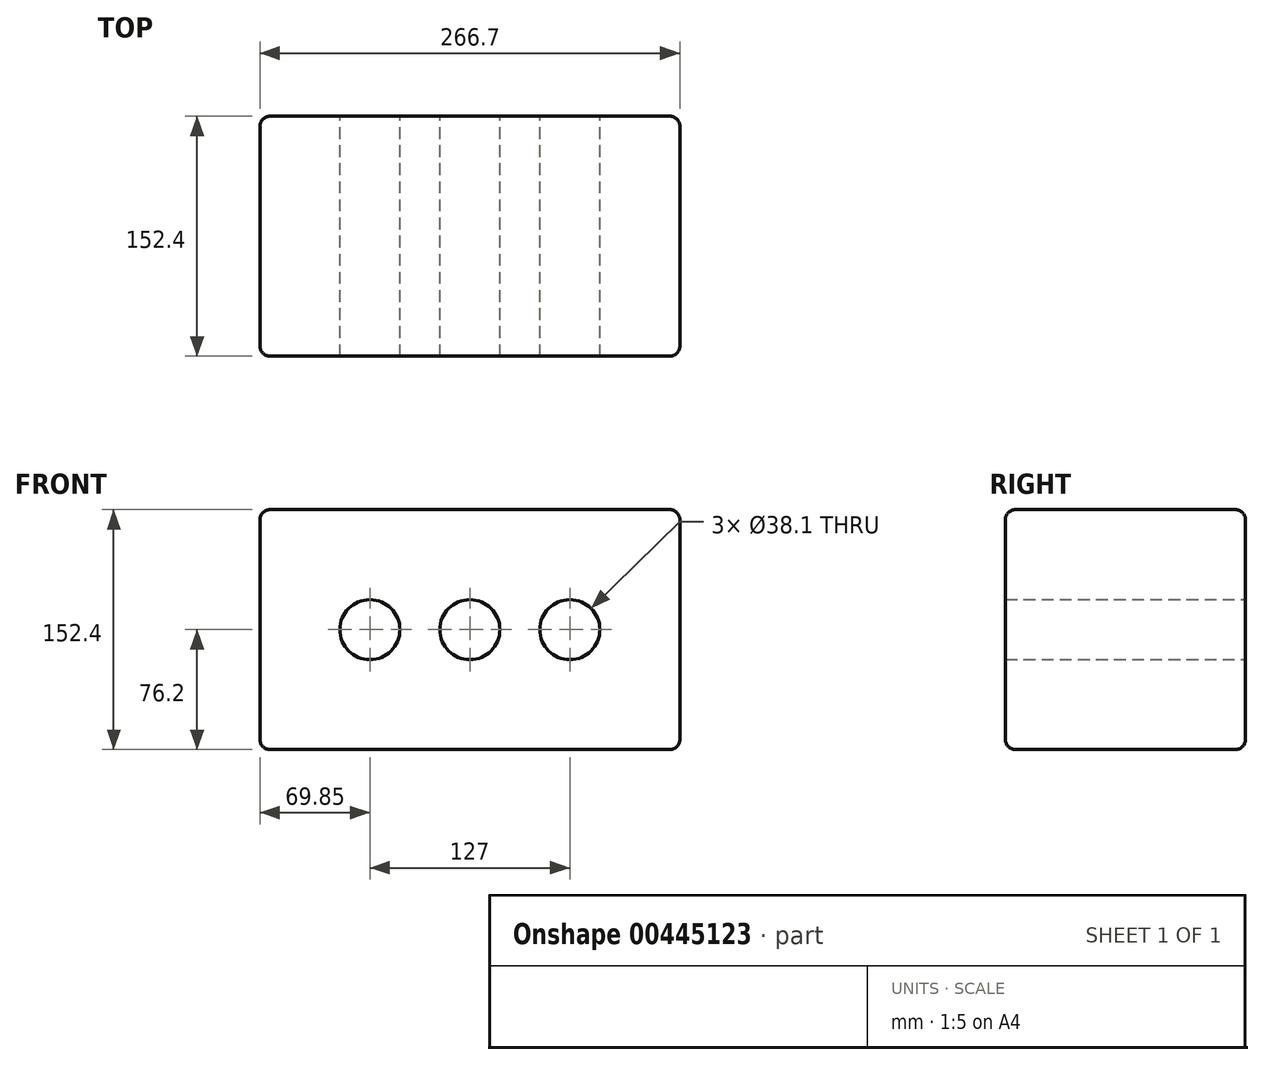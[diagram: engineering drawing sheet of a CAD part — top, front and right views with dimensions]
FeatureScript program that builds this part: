
annotation { "Feature Type Name" : "Feature", "Feature Type Description" : "" }
export const myFeature = defineFeature(function(context is Context, id is Id, definition is map)
    precondition{}
    {
        {
            var Q0;
            Q0=qCreatedBy(makeId("Front.planeOp"),FACE);
            var sketch = newSketch(context, id + "F0", { "sketchPlane" : qUnion([Q0])});
            skLineSegment(sketch, "E0.bottom", {"start": v(133.35, -76.2) * mm, "end": v(-133.35, -76.2) * mm});
            skLineSegment(sketch, "E0.top", {"start": v(133.35, 76.2) * mm, "end": v(-133.35, 76.2) * mm});
            skLineSegment(sketch, "E0.left", {"start": v(133.35, -76.2) * mm, "end": v(133.35, 76.2) * mm});
            skLineSegment(sketch, "E0.right", {"start": v(-133.35, -76.2) * mm, "end": v(-133.35, 76.2) * mm});
            skPoint(sketch, "E0.middle", {"position": v(0, 0) * mm});
            skCircle(sketch, "E1", {"center": v(-63.5, 0) * mm, "radius": 19.05 * mm});
            skCircle(sketch, "E2", {"center": v(0, 0) * mm, "radius": 19.05 * mm});
            skCircle(sketch, "E3", {"center": v(63.5, 0) * mm, "radius": 19.05 * mm});
            skLineSegment(sketch, "E4", {"start": v(-133.35, 0) * mm, "end": v(-82.55, 0) * mm});
            skLineSegment(sketch, "E5", {"start": v(-44.45, 0) * mm, "end": v(-19.05, 0) * mm});
            skLineSegment(sketch, "E6", {"start": v(19.05, 0) * mm, "end": v(44.45, 0) * mm});
            skLineSegment(sketch, "E7", {"start": v(82.55, 0) * mm, "end": v(133.35, 0) * mm});
            skLineSegment(sketch, "E8", {"start": v(-63.5, 0) * mm, "end": v(0, 0) * mm});
            skLineSegment(sketch, "E9", {"start": v(63.5, 0) * mm, "end": v(0, 0) * mm});
            skSolve(sketch);
        }
        {
            var Q0;
            {var subQ1=sQuery(id+"F0.wireOp",EDGE,"E0.bottom");Q0=makeQuery(id+"F0.imprint","IMPRINT",FACE,{"disambiguationData":[TD([[makeQuery(id+"F0.imprint","IMPRINT",EDGE,{"derivedFrom":subQ1}),-1.0]])]});}
            var Q1;
            {var subQ1=sQuery(id+"F0.wireOp",EDGE,"E0.top");Q1=makeQuery(id+"F0.imprint","IMPRINT",FACE,{"disambiguationData":[TD([[makeQuery(id+"F0.imprint","IMPRINT",EDGE,{"derivedFrom":subQ1}),1.0]])]});}
            extrude(context, id + "F1", {"entities" : qUnion([Q0, Q1]), "depth" : 152.4 * mm});
        }
        {
            var Q0;
            Q0=makeQuery(id+"F1.opExtrude","CAP_EDGE",EDGE,{"disambiguationData":[OSD([sQuery(id+"F0.wireOp",EDGE,"E0.top")])],"isStart":false});
            var Q1;
            Q1=makeQuery(id+"F1.opExtrude","CAP_EDGE",EDGE,{"disambiguationData":[OSD([sQuery(id+"F0.wireOp",EDGE,"E0.left")])],"isStart":false});
            var Q2;
            Q2=makeQuery(id+"F1.opExtrude","CAP_EDGE",EDGE,{"disambiguationData":[OSD([sQuery(id+"F0.wireOp",EDGE,"E0.right")])],"isStart":false});
            var Q3;
            Q3=makeQuery(id+"F1.opExtrude","CAP_EDGE",EDGE,{"disambiguationData":[OSD([sQuery(id+"F0.wireOp",EDGE,"E0.bottom")])],"isStart":false});
            var Q4;
            Q4=makeQuery(id+"F1.opExtrude","CAP_EDGE",EDGE,{"disambiguationData":[OSD([sQuery(id+"F0.wireOp",EDGE,"E0.left")])],"isStart":true});
            var Q5;
            Q5=makeQuery(id+"F1.opExtrude","SWEPT_EDGE",EDGE,{"disambiguationData":[OSD([sQuery(id+"F0.wireOp",EDGE,"E0.bottom"),sQuery(id+"F0.wireOp",EDGE,"E0.left")])]});
            var Q6;
            Q6=makeQuery(id+"F1.opExtrude","SWEPT_EDGE",EDGE,{"disambiguationData":[OSD([sQuery(id+"F0.wireOp",EDGE,"E0.top"),sQuery(id+"F0.wireOp",EDGE,"E0.left")])]});
            var Q7;
            Q7=makeQuery(id+"F1.opExtrude","SWEPT_FACE",FACE,{"disambiguationData":[OSD([sQuery(id+"F0.wireOp",EDGE,"E0.top")])]});
            var Q8;
            Q8=makeQuery(id+"F1.opExtrude","SWEPT_EDGE",EDGE,{"disambiguationData":[OSD([sQuery(id+"F0.wireOp",EDGE,"E0.bottom"),sQuery(id+"F0.wireOp",EDGE,"E0.right")])]});
            var Q9;
            Q9=makeQuery(id+"F1.opExtrude","CAP_EDGE",EDGE,{"disambiguationData":[OSD([sQuery(id+"F0.wireOp",EDGE,"E0.right")])],"isStart":true});
            var Q10;
            Q10=makeQuery(id+"F1.opExtrude","CAP_EDGE",EDGE,{"disambiguationData":[OSD([sQuery(id+"F0.wireOp",EDGE,"E0.bottom")])],"isStart":true});
            fillet(context, id + "F2", {"entities" : qUnion([Q0, Q1, Q2, Q3, Q4, Q5, Q6, Q7, Q8, Q9, Q10]), "radius" : 6.35 * mm, "tangentPropagation" : true, "allowEdgeOverflow" : false});
        }
    });
